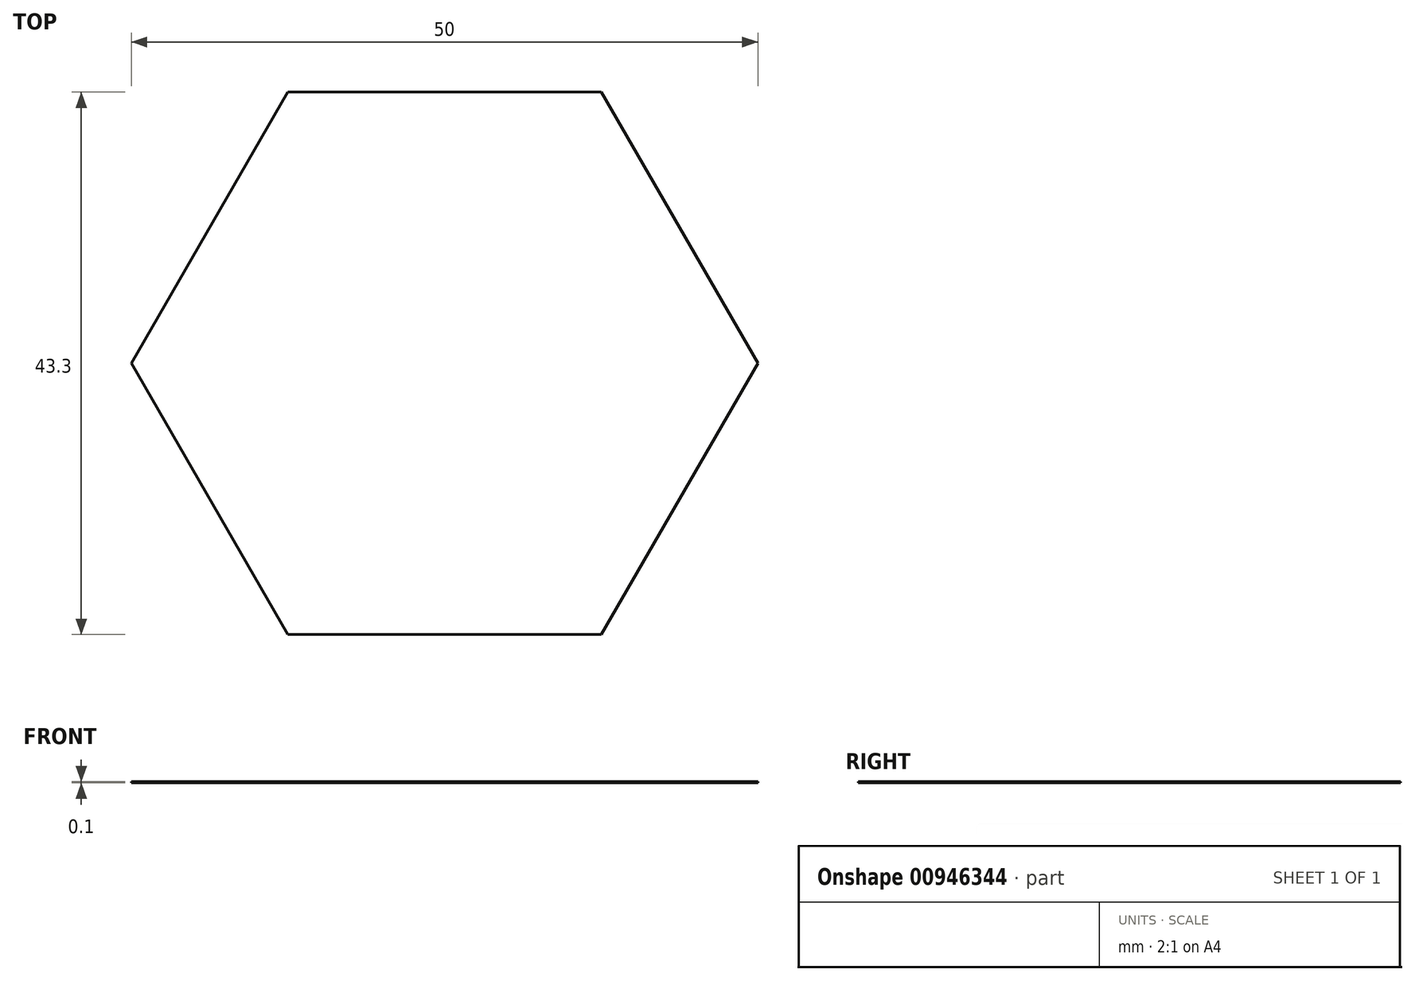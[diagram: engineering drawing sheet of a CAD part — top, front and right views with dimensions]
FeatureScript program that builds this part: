
annotation { "Feature Type Name" : "Feature", "Feature Type Description" : "" }
export const myFeature = defineFeature(function(context is Context, id is Id, definition is map)
    precondition{}
    {
        {
            var Q0;
            Q0=qCreatedBy(makeId("Top.planeOp"),FACE);
            var sketch = newSketch(context, id + "F0", { "sketchPlane" : qUnion([Q0])});
            skCircle(sketch, "E0.cCircle", {"center": v(0, 0) * mm, "radius": 21.65 * mm, "construction": true});
            skLineSegment(sketch, "E0.0", {"start": v(12.5, -21.65) * mm, "end": v(-12.5, -21.65) * mm});
            skLineSegment(sketch, "E0.1", {"start": v(-12.5, -21.65) * mm, "end": v(-25, 0) * mm});
            skLineSegment(sketch, "E0.2", {"start": v(-25, 0) * mm, "end": v(-12.5, 21.65) * mm});
            skLineSegment(sketch, "E0.3", {"start": v(-12.5, 21.65) * mm, "end": v(12.5, 21.65) * mm});
            skLineSegment(sketch, "E0.4", {"start": v(12.5, 21.65) * mm, "end": v(25, 0) * mm});
            skLineSegment(sketch, "E0.5", {"start": v(25, 0) * mm, "end": v(12.5, -21.65) * mm});
            skPoint(sketch, "E0.0.midPoint", {"position": v(0, -21.65) * mm});
            skSolve(sketch);
        }
        {
            var Q0;
            Q0=makeQuery(id+"F0.imprint","IMPRINT",FACE,{"disambiguationData":[TD([[makeQuery(id+"F0.imprint","IMPRINT",EDGE,{"derivedFrom":sQuery(id+"F0.wireOp",EDGE,"E0.0")}),-1.0]])]});
            extrude(context, id + "F1", {"entities" : qUnion([Q0]), "depth" : 0.1 * mm, "offsetDistance" : 25 * mm});
        }
    });
